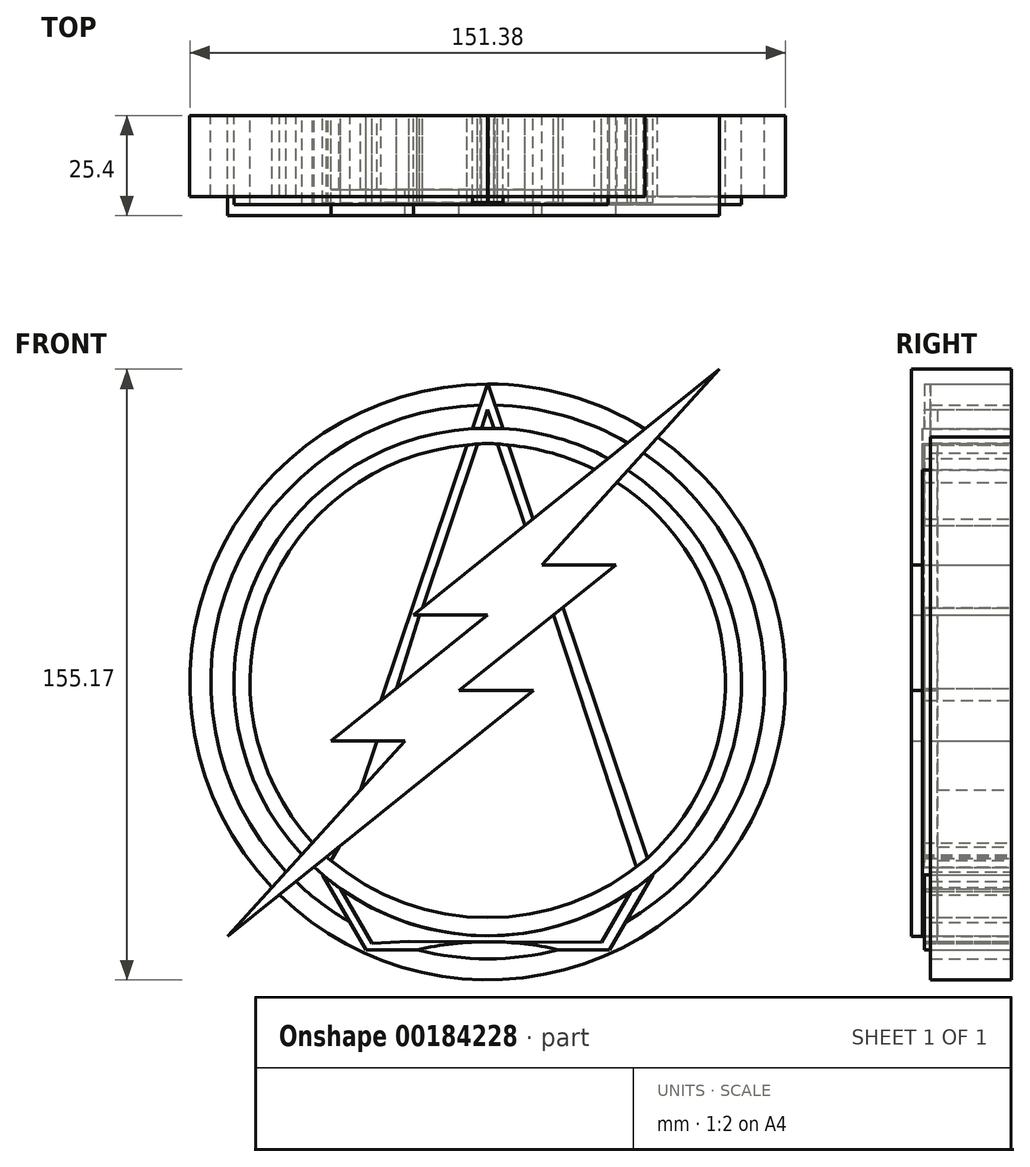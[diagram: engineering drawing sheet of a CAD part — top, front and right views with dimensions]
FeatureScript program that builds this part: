
annotation { "Feature Type Name" : "Feature", "Feature Type Description" : "" }
export const myFeature = defineFeature(function(context is Context, id is Id, definition is map)
    precondition{}
    {
        {
            var Q0;
            Q0=qCreatedBy(makeId("Front.planeOp"),FACE);
            var sketch = newSketch(context, id + "F0", { "sketchPlane" : qUnion([Q0])});
            skArc(sketch, "E0", {"start": v(-3.82, 64.37) * mm, "mid": v(-59.86, 24) * mm, "end": v(-47.23, -43.9) * mm});
            skLineSegment(sketch, "E1", {"start": v(-40.54, -44.77) * mm, "end": v(-40.25, -43.9) * mm});
            skLineSegment(sketch, "E2", {"start": v(0, 75.73) * mm, "end": v(3.82, 64.37) * mm});
            skArc(sketch, "E3", {"start": v(-5.24, 60.17) * mm, "mid": v(-56.3, 21.86) * mm, "end": v(-44.47, -40.87) * mm});
            skArc(sketch, "E4.trimOffspring", {"start": v(40.54, -44.77) * mm, "mid": v(60.2, 4.9) * mm, "end": v(32.77, 50.73) * mm});
            skLineSegment(sketch, "E5", {"start": v(-41.96, -48.97) * mm, "end": v(-30.95, -68.03) * mm});
            skLineSegment(sketch, "E6", {"start": v(-30.95, -68.03) * mm, "end": v(-17.94, -68.03) * mm});
            skLineSegment(sketch, "E7", {"start": v(30.95, -68.03) * mm, "end": v(41.96, -48.97) * mm});
            skLineSegment(sketch, "E8", {"start": v(58.82, 79.48) * mm, "end": v(-18.84, 17.02) * mm});
            skLineSegment(sketch, "E9", {"start": v(-18.84, 17.02) * mm, "end": v(0, 17.02) * mm});
            skLineSegment(sketch, "E10", {"start": v(0, 17.02) * mm, "end": v(-39.84, -15) * mm});
            skLineSegment(sketch, "E11", {"start": v(-39.84, -15) * mm, "end": v(-21, -15) * mm});
            skLineSegment(sketch, "E12", {"start": v(-7.26, -2.22) * mm, "end": v(32.62, 29.78) * mm});
            skLineSegment(sketch, "E13", {"start": v(32.62, 29.78) * mm, "end": v(13.78, 29.78) * mm});
            skLineSegment(sketch, "E14", {"start": v(13.78, 29.78) * mm, "end": v(58.82, 79.48) * mm});
            skLineSegment(sketch, "E15", {"start": v(-21, -15) * mm, "end": v(-66.08, -64.67) * mm});
            skLineSegment(sketch, "E16", {"start": v(-66.08, -64.67) * mm, "end": v(11.58, -2.22) * mm});
            skLineSegment(sketch, "E17", {"start": v(-7.26, -2.22) * mm, "end": v(11.58, -2.22) * mm});
            skLineSegment(sketch, "E18.trimOffspring", {"start": v(19.1, 18.93) * mm, "end": v(40.54, -44.77) * mm});
            skLineSegment(sketch, "E19.trimOffspring", {"start": v(-27.08, -4.75) * mm, "end": v(-5.24, 60.17) * mm});
            skArc(sketch, "E20.trimOffspring", {"start": v(-40.91, -44.43) * mm, "mid": v(-40.73, -44.6) * mm, "end": v(-40.54, -44.77) * mm});
            skArc(sketch, "E21.trimOffspring", {"start": v(-44.13, -47.02) * mm, "mid": v(50.6, -39.99) * mm, "end": v(35.55, 53.8) * mm});
            skArc(sketch, "E22", {"start": v(-40.54, -44.77) * mm, "mid": v(0, -59.87) * mm, "end": v(40.54, -44.77) * mm});
            skArc(sketch, "E23", {"start": v(-17.94, -68.03) * mm, "mid": v(0, -70.36) * mm, "end": v(17.94, -68.03) * mm});
            skArc(sketch, "E24.0", {"start": v(-52.94, -54.1) * mm, "mid": v(53.87, 53.17) * mm, "end": v(-54.79, -52.23) * mm});
            skArc(sketch, "E25.trimOffspring", {"start": v(35, -61.04) * mm, "mid": v(70.3, -2.68) * mm, "end": v(39.53, 58.2) * mm});
            skArc(sketch, "E26.trimOffspring", {"start": v(-48.75, -50.73) * mm, "mid": v(-42.19, -56.3) * mm, "end": v(-35, -61.04) * mm});
            skArc(sketch, "E27.trimOffspring", {"start": v(27.1, 53.97) * mm, "mid": v(16.46, 58.1) * mm, "end": v(5.24, 60.17) * mm});
            skArc(sketch, "E28.trimOffspring", {"start": v(30.58, 56.78) * mm, "mid": v(17.62, 62.04) * mm, "end": v(3.82, 64.37) * mm});
            skArc(sketch, "E29.trimOffspring", {"start": v(35.51, 60.74) * mm, "mid": v(19.27, 67.67) * mm, "end": v(1.82, 70.33) * mm});
            skArc(sketch, "E30.trimOffspring", {"start": v(-1.82, 70.33) * mm, "mid": v(-64.95, 27.04) * mm, "end": v(-51.2, -48.27) * mm});
            skLineSegment(sketch, "E31", {"start": v(58.82, 79.48) * mm, "end": v(2.56, 25.64) * mm});
            skLineSegment(sketch, "E32", {"start": v(2.56, 25.64) * mm, "end": v(-18.84, 17.02) * mm});
            skLineSegment(sketch, "E33", {"start": v(2.56, 25.64) * mm, "end": v(13.73, 25.64) * mm});
            skLineSegment(sketch, "E34", {"start": v(13.73, 25.64) * mm, "end": v(0, 17.02) * mm});
            skLineSegment(sketch, "E35", {"start": v(13.73, 25.64) * mm, "end": v(32.62, 29.78) * mm});
            skLineSegment(sketch, "E36", {"start": v(-39.84, -15) * mm, "end": v(-7.26, -2.22) * mm});
            skLineSegment(sketch, "E37", {"start": v(13.73, 25.64) * mm, "end": v(-21.03, -7.62) * mm});
            skLineSegment(sketch, "E38", {"start": v(-21.03, -7.62) * mm, "end": v(-7.26, -7.62) * mm});
            skLineSegment(sketch, "E39", {"start": v(-7.26, -7.62) * mm, "end": v(11.58, -2.22) * mm});
            skLineSegment(sketch, "E40", {"start": v(-7.26, -7.62) * mm, "end": v(-66.08, -64.67) * mm});
            skArc(sketch, "E41", {"start": v(28.63, 55.2) * mm, "mid": v(-49.44, 37.72) * mm, "end": v(-45.68, -42.2) * mm});
            skArc(sketch, "E42.trimOffspring", {"start": v(-42.32, -45.56) * mm, "mid": v(49, -38.29) * mm, "end": v(33.98, 52.07) * mm});
            skArc(sketch, "E43", {"start": v(3.82, 64.37) * mm, "mid": v(0, 64.4) * mm, "end": v(-3.82, 64.37) * mm});
            skArc(sketch, "E44", {"start": v(5.24, 60.17) * mm, "mid": v(0, 60.54) * mm, "end": v(-5.24, 60.17) * mm});
            skLineSegment(sketch, "E45.trimOffspring", {"start": v(-3.82, 64.37) * mm, "end": v(0, 75.73) * mm});
            skLineSegment(sketch, "E46.trimOffspring", {"start": v(5.24, 60.17) * mm, "end": v(11.53, 41.45) * mm});
            skPoint(sketch, "E47.endSnap0", {"position": v(-30.42, -15) * mm});
            skLineSegment(sketch, "E48", {"start": v(-30.42, -15) * mm, "end": v(-35.07, -30.5) * mm});
            skLineSegment(sketch, "E49", {"start": v(-32.33, -27.49) * mm, "end": v(-28.13, -15) * mm});
            skLineSegment(sketch, "E50", {"start": v(-23.16, -1.6) * mm, "end": v(-17.36, 17.02) * mm});
            skLineSegment(sketch, "E51", {"start": v(-16.58, 18.84) * mm, "end": v(-2.58, 60.45) * mm});
            skLineSegment(sketch, "E52", {"start": v(-1.6, 64.4) * mm, "end": v(0, 69.17) * mm});
            skLineSegment(sketch, "E53", {"start": v(0, 69.17) * mm, "end": v(1.6, 64.4) * mm});
            skLineSegment(sketch, "E54", {"start": v(2.46, 60.46) * mm, "end": v(9.42, 39.76) * mm});
            skLineSegment(sketch, "E55", {"start": v(16.66, 16.96) * mm, "end": v(37.73, -47.06) * mm});
            skLineSegment(sketch, "E56.trimOffspring", {"start": v(17.94, -68.03) * mm, "end": v(30.95, -68.03) * mm});
            skArc(sketch, "E57", {"start": v(17.94, -68.03) * mm, "mid": v(0, -66.01) * mm, "end": v(-17.94, -68.03) * mm});
            skLineSegment(sketch, "E58", {"start": v(-37.39, -52.54) * mm, "end": v(-29.34, -66.48) * mm});
            skLineSegment(sketch, "E59", {"start": v(-29.34, -66.48) * mm, "end": v(-19.95, -65.88) * mm});
            skLineSegment(sketch, "E60", {"start": v(-19.95, -65.88) * mm, "end": v(20.32, -66.14) * mm});
            skLineSegment(sketch, "E61", {"start": v(20.32, -66.14) * mm, "end": v(28.93, -66.19) * mm});
            skLineSegment(sketch, "E62", {"start": v(28.93, -66.19) * mm, "end": v(36.41, -53.22) * mm});
            skLineSegment(sketch, "E63", {"start": v(-37.82, -41.95) * mm, "end": v(-39.84, -45.37) * mm});
            skSolve(sketch);
        }
        {
            var Q0;
            {var subQ0=sQuery(id+"F0.wireOp",EDGE,"E35");Q0=makeQuery(id+"F0.imprint","IMPRINT",FACE,{"disambiguationData":[TD([[makeQuery(id+"F0.imprint","IMPRINT",EDGE,{"derivedFrom":subQ0}),-1.0]])]});}
            var Q1;
            {var subQ5=sQuery(id+"F0.wireOp",EDGE,"E34");Q1=makeQuery(id+"F0.imprint","IMPRINT",FACE,{"disambiguationData":[TD([[makeQuery(id+"F0.imprint","IMPRINT",EDGE,{"derivedFrom":subQ5}),1.0]])]});}
            var Q2;
            {var subQ0=sQuery(id+"F0.wireOp",EDGE,"E32");Q2=makeQuery(id+"F0.imprint","IMPRINT",FACE,{"disambiguationData":[TD([[makeQuery(id+"F0.imprint","IMPRINT",EDGE,{"derivedFrom":subQ0}),1.0]])]});}
            var Q3;
            {var subQ4=sQuery(id+"F0.wireOp",EDGE,"E13");Q3=makeQuery(id+"F0.imprint","IMPRINT",FACE,{"disambiguationData":[TD([[makeQuery(id+"F0.imprint","IMPRINT",EDGE,{"derivedFrom":subQ4}),1.0]])]});}
            var Q4;
            {var subQ0=sQuery(id+"F0.wireOp",EDGE,"E32");Q4=makeQuery(id+"F0.imprint","IMPRINT",FACE,{"disambiguationData":[TD([[makeQuery(id+"F0.imprint","IMPRINT",EDGE,{"derivedFrom":subQ0}),-1.0]])]});}
            var Q5;
            {var subQ1=sQuery(id+"F0.wireOp",EDGE,"E8");var subQ3=sQuery(id+"F0.wireOp",EDGE,"E24.0");var subQ4=makeQuery(id+"F0.imprint","INTERSECT",VERTEX,{"derivedFrom":[subQ1,subQ3]});Q5=makeQuery(id+"F0.imprint","IMPRINT",FACE,{"disambiguationData":[TD([[makeQuery(id+"F0.imprint","IMPRINT",EDGE,{"disambiguationData":[TD([[subQ4,1.0]])],"derivedFrom":subQ3}),-1.0]])]});}
            var Q6;
            {var subQ1=sQuery(id+"F0.wireOp",EDGE,"E14");var subQ3=sQuery(id+"F0.wireOp",EDGE,"E24.0");var subQ4=makeQuery(id+"F0.imprint","INTERSECT",VERTEX,{"derivedFrom":[subQ1,subQ3]});Q6=makeQuery(id+"F0.imprint","IMPRINT",FACE,{"disambiguationData":[TD([[makeQuery(id+"F0.imprint","IMPRINT",EDGE,{"disambiguationData":[TD([[subQ4,-1.0]])],"derivedFrom":subQ3}),-1.0]])]});}
            var Q7;
            {var subQ6=sQuery(id+"F0.wireOp",EDGE,"E39");Q7=makeQuery(id+"F0.imprint","IMPRINT",FACE,{"disambiguationData":[TD([[makeQuery(id+"F0.imprint","IMPRINT",EDGE,{"derivedFrom":subQ6}),-1.0]])]});}
            var Q8;
            {var subQ17=sQuery(id+"F0.wireOp",EDGE,"E38");Q8=makeQuery(id+"F0.imprint","IMPRINT",FACE,{"disambiguationData":[TD([[makeQuery(id+"F0.imprint","IMPRINT",EDGE,{"derivedFrom":subQ17}),-1.0]])]});}
            var Q9;
            {var subQ0=sQuery(id+"F0.wireOp",EDGE,"E17");Q9=makeQuery(id+"F0.imprint","IMPRINT",FACE,{"disambiguationData":[TD([[makeQuery(id+"F0.imprint","IMPRINT",EDGE,{"derivedFrom":subQ0}),-1.0]])]});}
            extrude(context, id + "F1", {"entities" : qUnion([Q0, Q1, Q2, Q3, Q4, Q5, Q6, Q7, Q8, Q9]), "depth" : 25.4 * mm});
        }
        {
            var Q0;
            {var subQ0=sQuery(id+"F0.wireOp",EDGE,"E51");Q0=makeQuery(id+"F0.imprint","IMPRINT",FACE,{"disambiguationData":[TD([[makeQuery(id+"F0.imprint","IMPRINT",EDGE,{"derivedFrom":subQ0}),-1.0]])]});}
            var Q1;
            {var subQ0=sQuery(id+"F0.wireOp",EDGE,"E52");Q1=makeQuery(id+"F0.imprint","IMPRINT",FACE,{"disambiguationData":[TD([[makeQuery(id+"F0.imprint","IMPRINT",EDGE,{"derivedFrom":subQ0}),-1.0]])]});}
            var Q2;
            {var subQ3=sQuery(id+"F0.wireOp",EDGE,"E17");Q2=makeQuery(id+"F0.imprint","IMPRINT",FACE,{"disambiguationData":[TD([[makeQuery(id+"F0.imprint","IMPRINT",EDGE,{"derivedFrom":subQ3}),1.0]])]});}
            var Q3;
            {var subQ3=sQuery(id+"F0.wireOp",EDGE,"E50");Q3=makeQuery(id+"F0.imprint","IMPRINT",FACE,{"disambiguationData":[TD([[makeQuery(id+"F0.imprint","IMPRINT",EDGE,{"derivedFrom":subQ3}),-1.0]])]});}
            var Q4;
            {var subQ3=sQuery(id+"F0.wireOp",EDGE,"E49");Q4=makeQuery(id+"F0.imprint","IMPRINT",FACE,{"disambiguationData":[TD([[makeQuery(id+"F0.imprint","IMPRINT",EDGE,{"derivedFrom":subQ3}),-1.0]])]});}
            extrude(context, id + "F2", {"entities" : qUnion([Q0, Q1, Q2, Q3, Q4]), "operationType" : NewBodyOperationType.ADD, "depth" : 18.8 * mm});
        }
        {
            var Q0;
            {var subQ3=sQuery(id+"F0.wireOp",EDGE,"E58");Q0=makeQuery(id+"F0.imprint","IMPRINT",FACE,{"disambiguationData":[TD([[makeQuery(id+"F0.imprint","IMPRINT",EDGE,{"derivedFrom":subQ3}),1.0]])]});}
            extrude(context, id + "F3", {"entities" : qUnion([Q0]), "depth" : 18.8 * mm});
        }
        {
            var Q0;
            {var subQ2=sQuery(id+"F0.wireOp",EDGE,"E0");Q0=makeQuery(id+"F0.imprint","IMPRINT",FACE,{"disambiguationData":[TD([[makeQuery(id+"F0.imprint","IMPRINT",EDGE,{"derivedFrom":subQ2}),1.0]])]});}
            var Q1;
            {var subQ5=sQuery(id+"F0.wireOp",EDGE,"E42.trimOffspring");Q1=makeQuery(id+"F0.imprint","IMPRINT",FACE,{"disambiguationData":[TD([[makeQuery(id+"F0.imprint","IMPRINT",EDGE,{"derivedFrom":subQ5}),-1.0]])]});}
            var Q2;
            {var subQ2=sQuery(id+"F0.wireOp",EDGE,"E3");Q2=makeQuery(id+"F0.imprint","IMPRINT",FACE,{"disambiguationData":[TD([[makeQuery(id+"F0.imprint","IMPRINT",EDGE,{"derivedFrom":subQ2}),-1.0]])]});}
            var Q3;
            {var subQ4=sQuery(id+"F0.wireOp",EDGE,"E4.trimOffspring");Q3=makeQuery(id+"F0.imprint","IMPRINT",FACE,{"disambiguationData":[TD([[makeQuery(id+"F0.imprint","IMPRINT",EDGE,{"derivedFrom":subQ4}),-1.0]])]});}
            extrude(context, id + "F4", {"entities" : qUnion([Q0, Q1, Q2, Q3]), "depth" : 22.6 * mm});
        }
        {
            var Q0;
            {var subQ3=sQuery(id+"F0.wireOp",EDGE,"E30.trimOffspring");Q0=makeQuery(id+"F0.imprint","IMPRINT",FACE,{"disambiguationData":[TD([[makeQuery(id+"F0.imprint","IMPRINT",EDGE,{"derivedFrom":subQ3}),-1.0]])]});}
            var Q1;
            {var subQ0=sQuery(id+"F0.wireOp",EDGE,"E29.trimOffspring");Q1=makeQuery(id+"F0.imprint","IMPRINT",FACE,{"disambiguationData":[TD([[makeQuery(id+"F0.imprint","IMPRINT",EDGE,{"derivedFrom":subQ0}),-1.0]])]});}
            var Q2;
            {var subQ9=sQuery(id+"F0.wireOp",EDGE,"E6");Q2=makeQuery(id+"F0.imprint","IMPRINT",FACE,{"disambiguationData":[TD([[makeQuery(id+"F0.imprint","IMPRINT",EDGE,{"derivedFrom":subQ9}),-1.0]])]});}
            extrude(context, id + "F5", {"entities" : qUnion([Q0, Q1, Q2]), "depth" : 20.57 * mm});
        }
        {
            var Q0;
            {var subQ0=sQuery(id+"F0.wireOp",EDGE,"E19.trimOffspring");Q0=makeQuery(id+"F0.imprint","IMPRINT",FACE,{"disambiguationData":[TD([[makeQuery(id+"F0.imprint","IMPRINT",EDGE,{"derivedFrom":subQ0}),-1.0]])]});}
            var Q1;
            {var subQ10=sQuery(id+"F0.wireOp",EDGE,"E52");Q1=makeQuery(id+"F0.imprint","IMPRINT",FACE,{"disambiguationData":[TD([[makeQuery(id+"F0.imprint","IMPRINT",EDGE,{"derivedFrom":subQ10}),1.0]])]});}
            var Q2;
            {var subQ0=sQuery(id+"F0.wireOp",EDGE,"E46.trimOffspring");Q2=makeQuery(id+"F0.imprint","IMPRINT",FACE,{"disambiguationData":[TD([[makeQuery(id+"F0.imprint","IMPRINT",EDGE,{"derivedFrom":subQ0}),-1.0]])]});}
            var Q3;
            {var subQ0=sQuery(id+"F0.wireOp",EDGE,"E18.trimOffspring");Q3=makeQuery(id+"F0.imprint","IMPRINT",FACE,{"disambiguationData":[TD([[makeQuery(id+"F0.imprint","IMPRINT",EDGE,{"derivedFrom":subQ0}),-1.0]])]});}
            var Q4;
            {var subQ0=sQuery(id+"F0.wireOp",EDGE,"E56.trimOffspring");Q4=makeQuery(id+"F0.imprint","IMPRINT",FACE,{"disambiguationData":[TD([[makeQuery(id+"F0.imprint","IMPRINT",EDGE,{"derivedFrom":subQ0}),1.0]])]});}
            var Q5;
            {var subQ4=sQuery(id+"F0.wireOp",EDGE,"E6");Q5=makeQuery(id+"F0.imprint","IMPRINT",FACE,{"disambiguationData":[TD([[makeQuery(id+"F0.imprint","IMPRINT",EDGE,{"derivedFrom":subQ4}),1.0]])]});}
            extrude(context, id + "F6", {"entities" : qUnion([Q0, Q1, Q2, Q3, Q4, Q5]), "depth" : 22.1 * mm});
        }
    });
